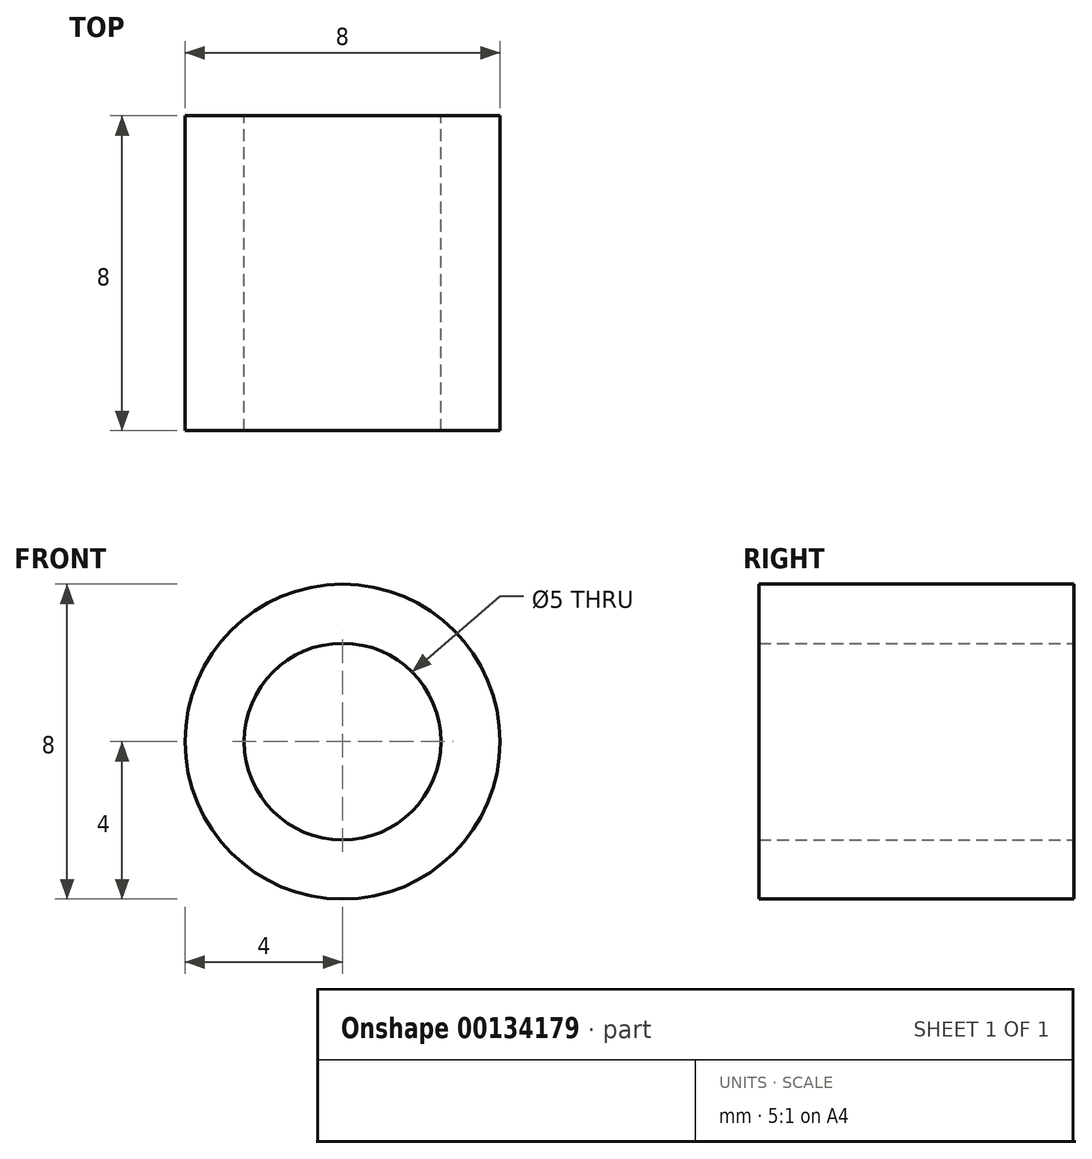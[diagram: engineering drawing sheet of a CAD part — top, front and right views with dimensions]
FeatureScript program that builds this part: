
annotation { "Feature Type Name" : "Feature", "Feature Type Description" : "" }
export const myFeature = defineFeature(function(context is Context, id is Id, definition is map)
    precondition{}
    {
        {
            var Q0;
            Q0=qCreatedBy(makeId("Front.planeOp"),FACE);
            var sketch = newSketch(context, id + "F0", { "sketchPlane" : qUnion([Q0])});
            skCircle(sketch, "E0", {"center": v(0, 0) * mm, "radius": 2.5 * mm});
            skCircle(sketch, "E1", {"center": v(0, 0) * mm, "radius": 4 * mm});
            skSolve(sketch);
        }
        {
            var Q0;
            Q0=makeQuery(id+"F0.imprint","IMPRINT",FACE,{"disambiguationData":[TD([[makeQuery(id+"F0.imprint","IMPRINT",EDGE,{"derivedFrom":sQuery(id+"F0.wireOp",EDGE,"E0")}),-1.0]])]});
            extrude(context, id + "F1", {"entities" : qUnion([Q0]), "depth" : 8 * mm});
        }
    });
